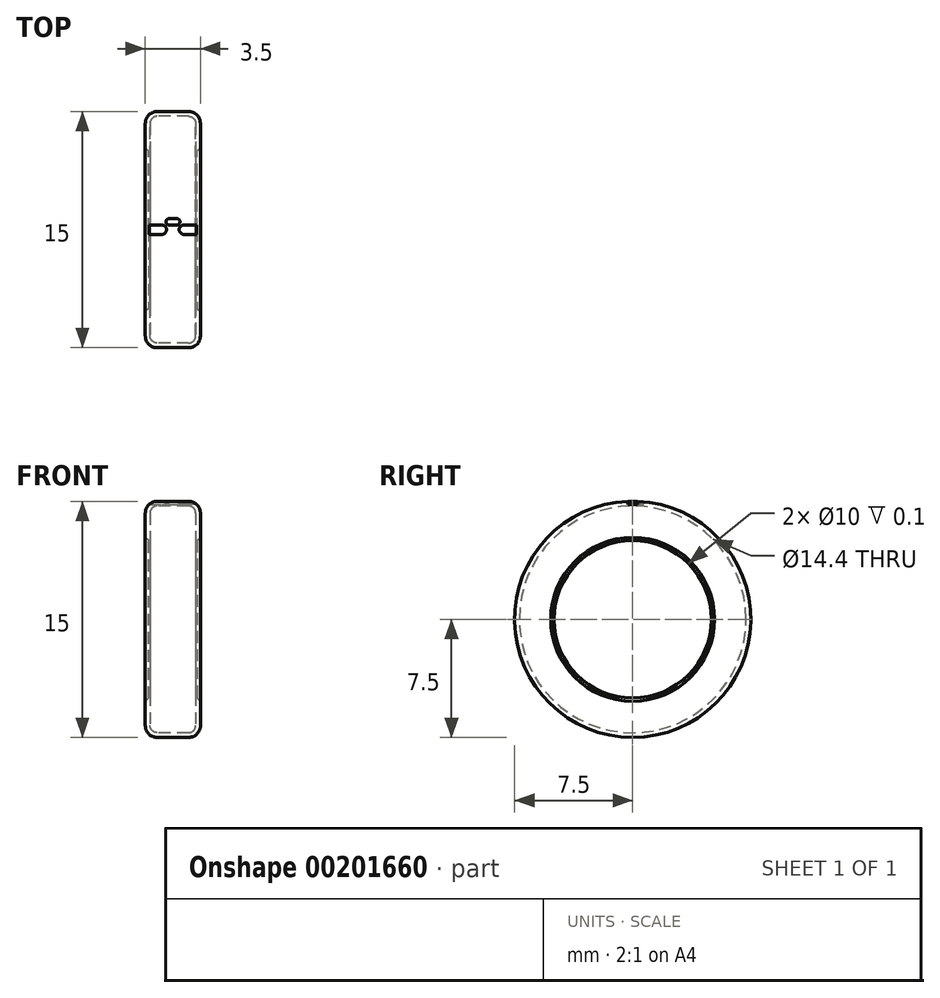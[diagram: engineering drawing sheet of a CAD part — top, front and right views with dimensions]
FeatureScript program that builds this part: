
annotation { "Feature Type Name" : "Feature", "Feature Type Description" : "" }
export const myFeature = defineFeature(function(context is Context, id is Id, definition is map)
    precondition{}
    {
        {
            var Q0;
            Q0=qCreatedBy(makeId("Front.planeOp"),FACE);
            var sketch = newSketch(context, id + "F0", { "sketchPlane" : qUnion([Q0])});
            skLineSegment(sketch, "E0", {"start": v(-29.59, 0) * mm, "end": v(30.89, 0) * mm, "construction": true});
            skLineSegment(sketch, "E1", {"start": v(0, 29.21) * mm, "end": v(0, -29.1) * mm, "construction": true});
            skLineSegment(sketch, "E2", {"start": v(0, -7.5) * mm, "end": v(-1, -7.5) * mm});
            skLineSegment(sketch, "E3", {"start": v(-1.75, -6.75) * mm, "end": v(-1.75, -5) * mm});
            skLineSegment(sketch, "E4", {"start": v(-1.75, -5) * mm, "end": v(-1.45, -5) * mm});
            skLineSegment(sketch, "E5", {"start": v(-1.45, -5) * mm, "end": v(-1.45, -6.75) * mm});
            skLineSegment(sketch, "E6", {"start": v(-1, -7.2) * mm, "end": v(0, -7.2) * mm});
            skPoint(sketch, "E7.visualSharp", {"position": v(-1.75, -7.5) * mm});
            skArc(sketch, "E7.filletArc", {"start": v(-1.75, -6.75) * mm, "mid": v(-1.53, -7.28) * mm, "end": v(-1, -7.5) * mm});
            skPoint(sketch, "E8.visualSharp", {"position": v(-1.45, -7.2) * mm});
            skArc(sketch, "E8.filletArc", {"start": v(-1.45, -6.75) * mm, "mid": v(-1.32, -7.07) * mm, "end": v(-1, -7.2) * mm});
            skLineSegment(sketch, "E9.MirrorCS", {"start": v(1.75, -5) * mm, "end": v(1.45, -5) * mm});
            skArc(sketch, "E10.MirrorCS", {"start": v(1.45, -6.75) * mm, "mid": v(1.32, -7.07) * mm, "end": v(1, -7.2) * mm});
            skArc(sketch, "E11.MirrorCS", {"start": v(1.75, -6.75) * mm, "mid": v(1.53, -7.28) * mm, "end": v(1, -7.5) * mm});
            skLineSegment(sketch, "E12.MirrorCS", {"start": v(1.45, -5) * mm, "end": v(1.45, -6.75) * mm});
            skPoint(sketch, "E13.MirrorP", {"position": v(1.75, -7.5) * mm});
            skLineSegment(sketch, "E14.MirrorCS", {"start": v(1.75, -6.75) * mm, "end": v(1.75, -5) * mm});
            skPoint(sketch, "E15.MirrorP", {"position": v(1.45, -7.2) * mm});
            skLineSegment(sketch, "E16.MirrorCS", {"start": v(1, -7.2) * mm, "end": v(0, -7.2) * mm});
            skLineSegment(sketch, "E17.MirrorCS", {"start": v(0, -7.5) * mm, "end": v(1, -7.5) * mm});
            skSolve(sketch);
        }
        {
            var Q0;
            Q0 = qSketchRegion(id + "F0", true);
            var Q1;
            Q1=sQuery(id+"F0.wireOp",EDGE,"E0");
            revolve(context, id + "F1", {"entities" : qUnion([Q0]), "axis" : qUnion([Q1]), "revolveType" : RevolveType.FULL});
        }
        {
            var Q0;
            Q0=qCreatedBy(makeId("Top.planeOp"),FACE);
            cPlane(context, id + "F2", {"entities" : qUnion([Q0]), "cplaneType" : CPlaneType.OFFSET, "offset" : 7.5 * mm, "width" : 150 * mm, "height" : 150 * mm});
        }
        {
            var Q0;
            Q0=qCreatedBy(id+"F2.planeOp",FACE);
            var sketch = newSketch(context, id + "F3", { "sketchPlane" : qUnion([Q0])});
            skLineSegment(sketch, "E18", {"start": v(-0.25, 0.5) * mm, "end": v(0.25, 0.5) * mm});
            skArc(sketch, "E19.0.startCap", {"start": v(-0.25, 0.3) * mm, "mid": v(-0.45, 0.5) * mm, "end": v(-0.25, 0.7) * mm});
            skArc(sketch, "E19.0.endCap", {"start": v(0.25, 0.7) * mm, "mid": v(0.45, 0.5) * mm, "end": v(0.25, 0.3) * mm});
            skLineSegment(sketch, "E19.0.left", {"start": v(-0.25, 0.7) * mm, "end": v(0.25, 0.7) * mm});
            skLineSegment(sketch, "E19.0.right", {"start": v(-0.25, 0.3) * mm, "end": v(0.25, 0.3) * mm});
            skLineSegment(sketch, "E20", {"start": v(0, 0) * mm, "end": v(0, 0.5) * mm, "construction": true});
            skArc(sketch, "E21", {"start": v(-0.7, -0.3) * mm, "mid": v(-0.4, 0) * mm, "end": v(-0.7, 0.3) * mm});
            skLineSegment(sketch, "E22", {"start": v(-0.7, 0.3) * mm, "end": v(-1.7, 0.3) * mm});
            skLineSegment(sketch, "E23", {"start": v(-1.7, 0.3) * mm, "end": v(-1.7, -0.3) * mm});
            skLineSegment(sketch, "E24", {"start": v(-1.7, -0.3) * mm, "end": v(-0.7, -0.3) * mm});
            skLineSegment(sketch, "E25.MirrorCS", {"start": v(1.7, -0.3) * mm, "end": v(0.7, -0.3) * mm});
            skLineSegment(sketch, "E26.MirrorCS", {"start": v(1.7, 0.3) * mm, "end": v(1.7, -0.3) * mm});
            skLineSegment(sketch, "E27.MirrorCS", {"start": v(0.7, 0.3) * mm, "end": v(1.7, 0.3) * mm});
            skArc(sketch, "E28.MirrorCS", {"start": v(0.7, -0.3) * mm, "mid": v(0.4, 0) * mm, "end": v(0.7, 0.3) * mm});
            skSolve(sketch);
        }
        {
            var Q0;
            Q0 = qSketchRegion(id + "F3", true);
            extrude(context, id + "F4", {"entities" : qUnion([Q0]), "operationType" : NewBodyOperationType.REMOVE, "oppositeDirection" : true, "depth" : .2 * mm});
        }
        {
            var Q0;
            Q0=makeQuery(id+"F1.opRevolve","SWEPT_EDGE",EDGE,{"disambiguationData":[OSD([sQuery(id+"F0.wireOp",EDGE,"E3"),sQuery(id+"F0.wireOp",EDGE,"E4")])]});
            var Q1;
            Q1=makeQuery(id+"F1.opRevolve","SWEPT_EDGE",EDGE,{"disambiguationData":[OSD([sQuery(id+"F0.wireOp",EDGE,"E9.MirrorCS"),sQuery(id+"F0.wireOp",EDGE,"E14.MirrorCS")])]});
            chamfer(context, id + "F5", {"entities" : qUnion([Q0, Q1]), "width" : .2 * mm, "tangentPropagation" : true});
        }
    });
